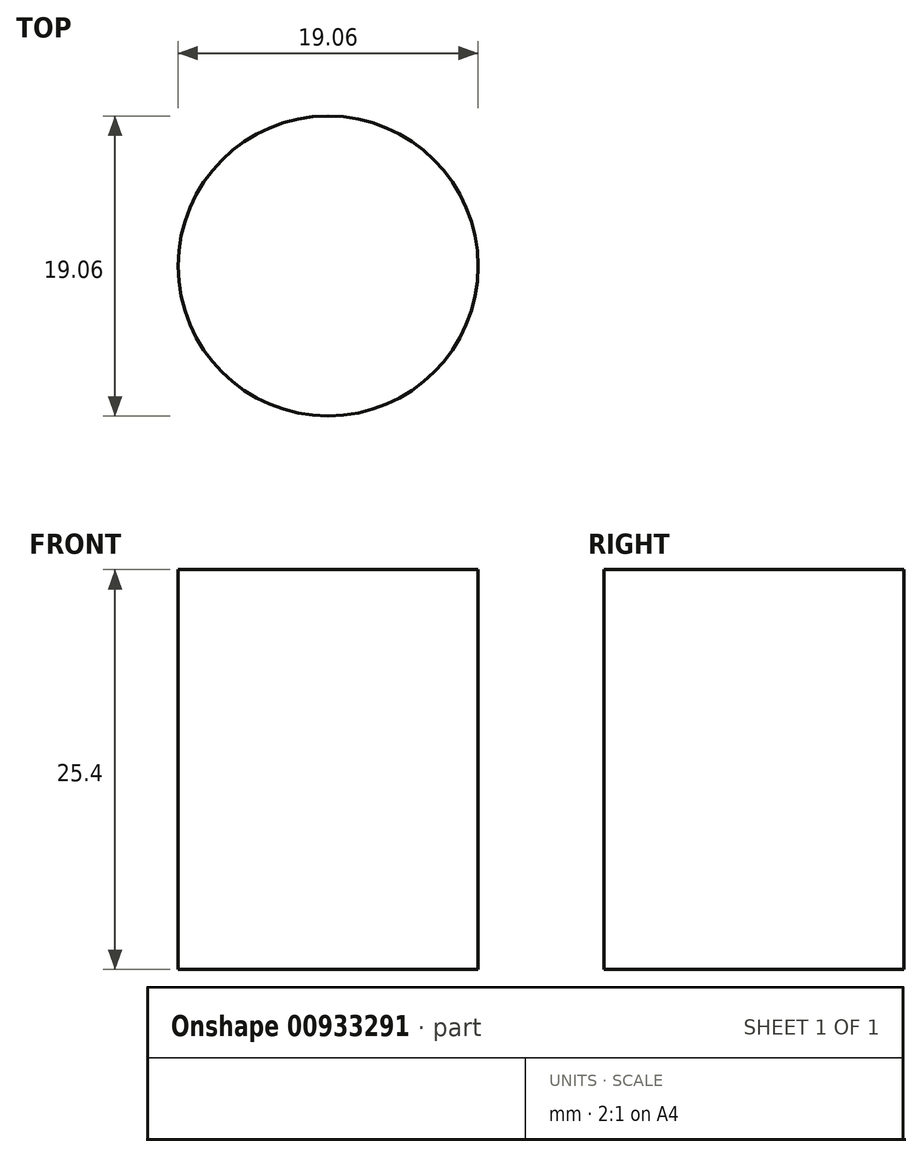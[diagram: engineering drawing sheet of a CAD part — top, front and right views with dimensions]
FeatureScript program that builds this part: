
annotation { "Feature Type Name" : "Feature", "Feature Type Description" : "" }
export const myFeature = defineFeature(function(context is Context, id is Id, definition is map)
    precondition{}
    {
        {
            var Q0;
            Q0=qCreatedBy(makeId("Top.planeOp"),FACE);
            var sketch = newSketch(context, id + "F0", { "sketchPlane" : qUnion([Q0])});
            skCircle(sketch, "E0", {"center": v(0, 0) * mm, "radius": 9.53 * mm});
            skSolve(sketch);
        }
        {
            var Q0;
            Q0 = qSketchRegion(id + "F0", true);
            extrude(context, id + "F1", {"entities" : qUnion([Q0]), "depth" : 25.4 * mm, "offsetDistance" : 25.4 * mm});
        }
    });
